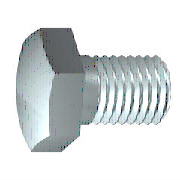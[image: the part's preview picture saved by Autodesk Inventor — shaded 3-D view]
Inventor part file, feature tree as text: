
AUTODESK INVENTOR PART (.ipt)
format: ipt  version: 2013 (Build 170138000, 138)  size: 187,392 bytes
history: native  units: mm (DEFAULTED — no unit token found)
features: sketch x2, extrude x1, chamfer x1, plane x1
ambient origin geometry x7: Origin, YZ Plane, XZ Plane, X Axis, Y Axis, Z Axis, Center Point
bodies: Solid1 (feature_tree), Body (feature_tree)
feature tree (5):
  extrude  "Head"  TaperAngle=90.0deg  [1 undecoded]
  chamfer  "Chamfer1"  [1 undecoded]
  plane  "Work Plane1"
  sketch  "Sketch1"  dims[d2=8.0mm d12=90.0deg]
  sketch  "Sketch2"  dims[d3=5.68mm d4=0.0mm d21=90.0deg d6=0.766813mm d7=0.766912mm d8=0.0mm d11=13.0mm d15=22.0mm d16=0.0mm d55=45.0deg d58=0.0mm d59=35.0mm d65=13.0mm d67=30.0deg d68=15.6mm d69=5.68mm d71=0.1mm d73=0.0mm]
note: 2 required parameter values undecoded (feature->parameter linkage not recoverable at this tier; creation-order binding heuristic only, values carry confidence <= 0.55)
